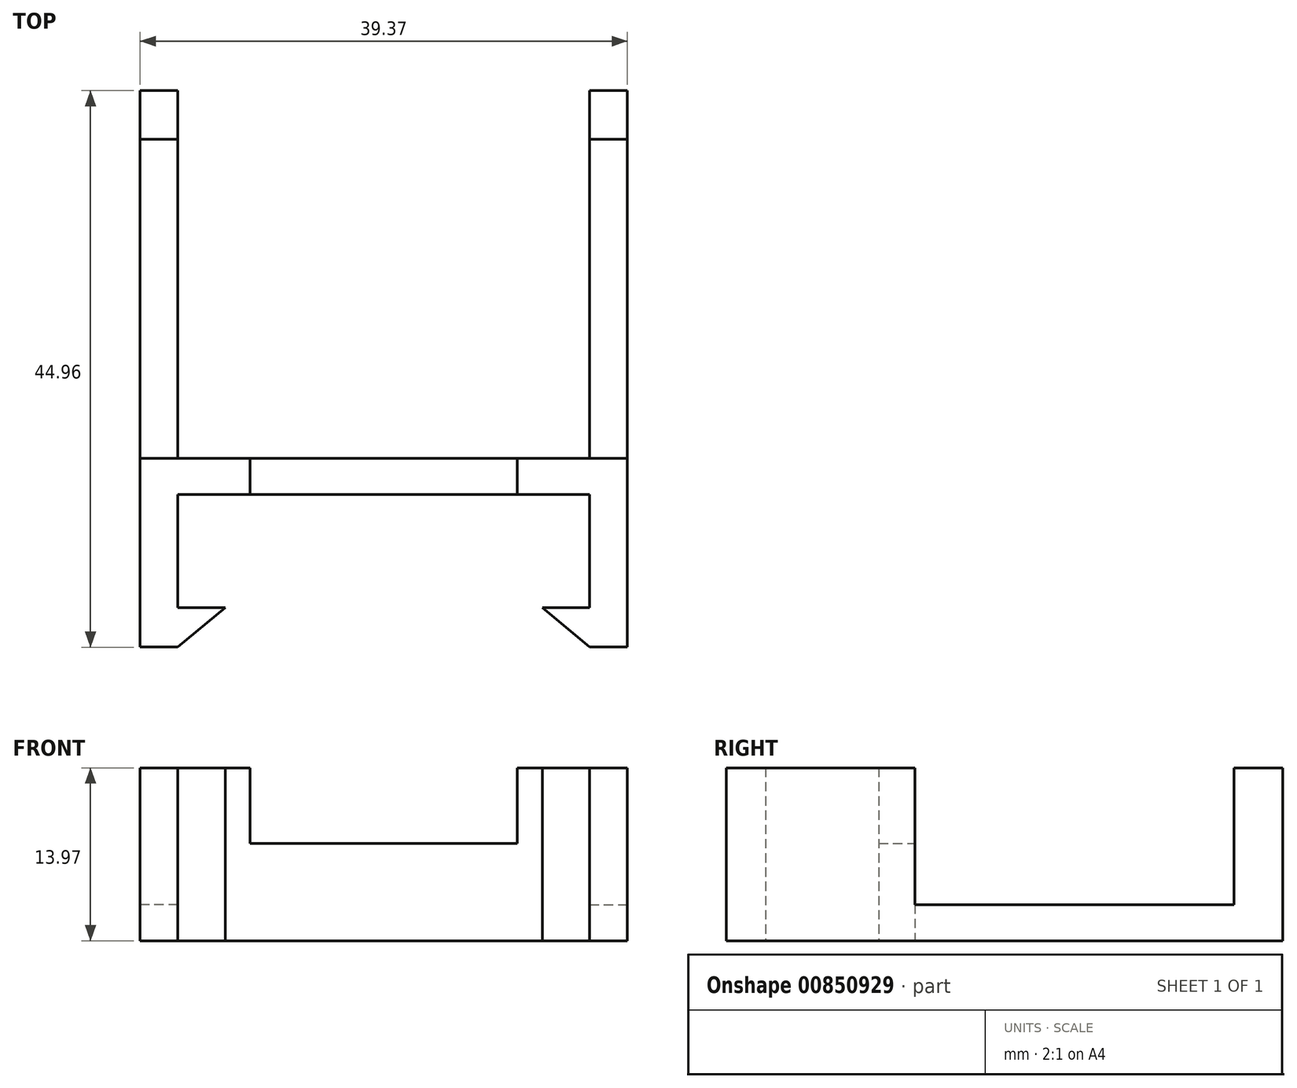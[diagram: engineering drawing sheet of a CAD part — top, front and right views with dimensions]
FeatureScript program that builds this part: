
annotation { "Feature Type Name" : "Feature", "Feature Type Description" : "" }
export const myFeature = defineFeature(function(context is Context, id is Id, definition is map)
    precondition{}
    {
        {
            var Q0;
            Q0=qCreatedBy(makeId("Top.planeOp"),FACE);
            var sketch = newSketch(context, id + "F0", { "sketchPlane" : qUnion([Q0])});
            skLineSegment(sketch, "E0", {"start": v(-3.05, 32.64) * mm, "end": v(0, 32.64) * mm});
            skLineSegment(sketch, "E1", {"start": v(0, 32.64) * mm, "end": v(0, 28.7) * mm});
            skLineSegment(sketch, "E2", {"start": v(0, 28.7) * mm, "end": v(-3.05, 28.7) * mm});
            skLineSegment(sketch, "E3", {"start": v(-3.05, 32.64) * mm, "end": v(-3.05, 28.7) * mm});
            skLineSegment(sketch, "E4", {"start": v(-3.05, 2.92) * mm, "end": v(-3.05, 28.7) * mm});
            skLineSegment(sketch, "E5", {"start": v(-3.05, 2.92) * mm, "end": v(0, 2.92) * mm});
            skLineSegment(sketch, "E6", {"start": v(0, 2.92) * mm, "end": v(-8.9, 2.92) * mm});
            skLineSegment(sketch, "E7", {"start": v(-8.9, 0) * mm, "end": v(-8.9, 2.92) * mm});
            skLineSegment(sketch, "E8", {"start": v(-3.05, 2.92) * mm, "end": v(-3.05, 2.92) * mm});
            skLineSegment(sketch, "E9", {"start": v(-8.9, 0) * mm, "end": v(-3.05, 0) * mm});
            skLineSegment(sketch, "E10", {"start": v(0, 2.92) * mm, "end": v(0, 28.7) * mm});
            skLineSegment(sketch, "E11", {"start": v(0, -12.32) * mm, "end": v(0, -9.14) * mm});
            skLineSegment(sketch, "E12", {"start": v(0, 2.92) * mm, "end": v(0, -12.32) * mm});
            skLineSegment(sketch, "E13", {"start": v(-3.05, 0) * mm, "end": v(-3.05, -9.14) * mm});
            skLineSegment(sketch, "E14", {"start": v(-8.9, 0) * mm, "end": v(-19.69, 0) * mm});
            skLineSegment(sketch, "E15", {"start": v(-8.9, 2.92) * mm, "end": v(-19.69, 2.92) * mm});
            skLineSegment(sketch, "E16", {"start": v(-19.69, 2.92) * mm, "end": v(-19.69, 0) * mm});
            skLineSegment(sketch, "E17.MirrorCS", {"start": v(-36.32, 32.64) * mm, "end": v(-39.37, 32.64) * mm});
            skLineSegment(sketch, "E18.MirrorCS", {"start": v(-36.32, 32.64) * mm, "end": v(-36.32, 28.7) * mm});
            skLineSegment(sketch, "E19.MirrorCS", {"start": v(-36.32, 2.92) * mm, "end": v(-39.37, 2.92) * mm});
            skLineSegment(sketch, "E20.MirrorCS", {"start": v(-30.48, 0) * mm, "end": v(-30.48, 2.92) * mm});
            skLineSegment(sketch, "E21.MirrorCS", {"start": v(-39.37, 32.64) * mm, "end": v(-39.37, 28.7) * mm});
            skLineSegment(sketch, "E22.MirrorCS", {"start": v(-39.37, 28.7) * mm, "end": v(-36.32, 28.7) * mm});
            skLineSegment(sketch, "E23.MirrorCS", {"start": v(-39.37, -12.32) * mm, "end": v(-39.37, -9.14) * mm});
            skLineSegment(sketch, "E24.MirrorCS", {"start": v(-30.48, 0) * mm, "end": v(-36.32, 0) * mm});
            skLineSegment(sketch, "E25.MirrorCS", {"start": v(-39.37, 2.92) * mm, "end": v(-39.37, -12.32) * mm});
            skLineSegment(sketch, "E26.MirrorCS", {"start": v(-36.32, 2.92) * mm, "end": v(-36.32, 28.7) * mm});
            skLineSegment(sketch, "E27.MirrorCS", {"start": v(-36.32, 2.92) * mm, "end": v(-36.32, 2.92) * mm});
            skLineSegment(sketch, "E28.MirrorCS", {"start": v(-39.37, 2.92) * mm, "end": v(-30.48, 2.92) * mm});
            skLineSegment(sketch, "E29.MirrorCS", {"start": v(-30.48, 2.92) * mm, "end": v(-19.69, 2.92) * mm});
            skLineSegment(sketch, "E30.MirrorCS", {"start": v(-36.32, 0) * mm, "end": v(-36.32, -9.14) * mm});
            skLineSegment(sketch, "E31.MirrorCS", {"start": v(-39.37, 2.92) * mm, "end": v(-39.37, 28.7) * mm});
            skLineSegment(sketch, "E32.MirrorCS", {"start": v(-30.48, 0) * mm, "end": v(-19.69, 0) * mm});
            skLineSegment(sketch, "E33", {"start": v(-3.05, -9.14) * mm, "end": v(-6.88, -9.14) * mm});
            skLineSegment(sketch, "E34", {"start": v(-6.88, -9.14) * mm, "end": v(-3.05, -12.32) * mm});
            skLineSegment(sketch, "E35", {"start": v(-3.05, -12.32) * mm, "end": v(0, -12.32) * mm});
            skLineSegment(sketch, "E36", {"start": v(-36.32, -9.14) * mm, "end": v(-32.49, -9.14) * mm});
            skLineSegment(sketch, "E37", {"start": v(-32.49, -9.14) * mm, "end": v(-36.32, -12.32) * mm});
            skLineSegment(sketch, "E38", {"start": v(-39.37, -12.32) * mm, "end": v(-36.32, -12.32) * mm});
            skSolve(sketch);
        }
        {
            var Q0;
            Q0=makeQuery(id+"F0.imprint","IMPRINT",FACE,{"disambiguationData":[TD([[makeQuery(id+"F0.imprint","IMPRINT",EDGE,{"derivedFrom":sQuery(id+"F0.wireOp",EDGE,"E16")}),-1.0]])]});
            var Q1;
            Q1=makeQuery(id+"F0.imprint","IMPRINT",FACE,{"disambiguationData":[TD([[makeQuery(id+"F0.imprint","IMPRINT",EDGE,{"derivedFrom":sQuery(id+"F0.wireOp",EDGE,"E7")}),1.0]])]});
            extrude(context, id + "F1", {"entities" : qUnion([Q0, Q1]), "depth" : 7.87 * mm, "offsetDistance" : 25.4 * mm});
        }
        {
            var Q0;
            {var subQ0=sQuery(id+"F0.wireOp",EDGE,"E7");Q0=makeQuery(id+"F0.imprint","IMPRINT",FACE,{"disambiguationData":[TD([[makeQuery(id+"F0.imprint","IMPRINT",EDGE,{"derivedFrom":subQ0}),-1.0]])]});}
            var Q1;
            {var subQ5=sQuery(id+"F0.wireOp",EDGE,"E20.MirrorCS");Q1=makeQuery(id+"F0.imprint","IMPRINT",FACE,{"disambiguationData":[TD([[makeQuery(id+"F0.imprint","IMPRINT",EDGE,{"derivedFrom":subQ5}),1.0]])]});}
            extrude(context, id + "F2", {"entities" : qUnion([Q0, Q1]), "operationType" : NewBodyOperationType.ADD, "depth" : 13.97 * mm, "offsetDistance" : 25.4 * mm});
        }
        {
            var Q0;
            Q0=makeQuery(id+"F0.imprint","IMPRINT",FACE,{"disambiguationData":[TD([[makeQuery(id+"F0.imprint","IMPRINT",EDGE,{"derivedFrom":sQuery(id+"F0.wireOp",EDGE,"E2")}),1.0]])]});
            var Q1;
            Q1=makeQuery(id+"F0.imprint","IMPRINT",FACE,{"disambiguationData":[TD([[makeQuery(id+"F0.imprint","IMPRINT",EDGE,{"derivedFrom":sQuery(id+"F0.wireOp",EDGE,"E22.MirrorCS")}),-1.0]])]});
            extrude(context, id + "F3", {"entities" : qUnion([Q0, Q1]), "operationType" : NewBodyOperationType.ADD, "depth" : 2.92 * mm, "offsetDistance" : 25.4 * mm});
        }
        {
            var Q0;
            Q0=makeQuery(id+"F0.imprint","IMPRINT",FACE,{"disambiguationData":[TD([[makeQuery(id+"F0.imprint","IMPRINT",EDGE,{"derivedFrom":sQuery(id+"F0.wireOp",EDGE,"E1")}),-1.0]])]});
            var Q1;
            Q1=makeQuery(id+"F0.imprint","IMPRINT",FACE,{"disambiguationData":[TD([[makeQuery(id+"F0.imprint","IMPRINT",EDGE,{"derivedFrom":sQuery(id+"F0.wireOp",EDGE,"E18.MirrorCS")}),-1.0]])]});
            extrude(context, id + "F4", {"entities" : qUnion([Q0, Q1]), "operationType" : NewBodyOperationType.ADD, "depth" : 13.97 * mm, "offsetDistance" : 25.4 * mm});
        }
    });
